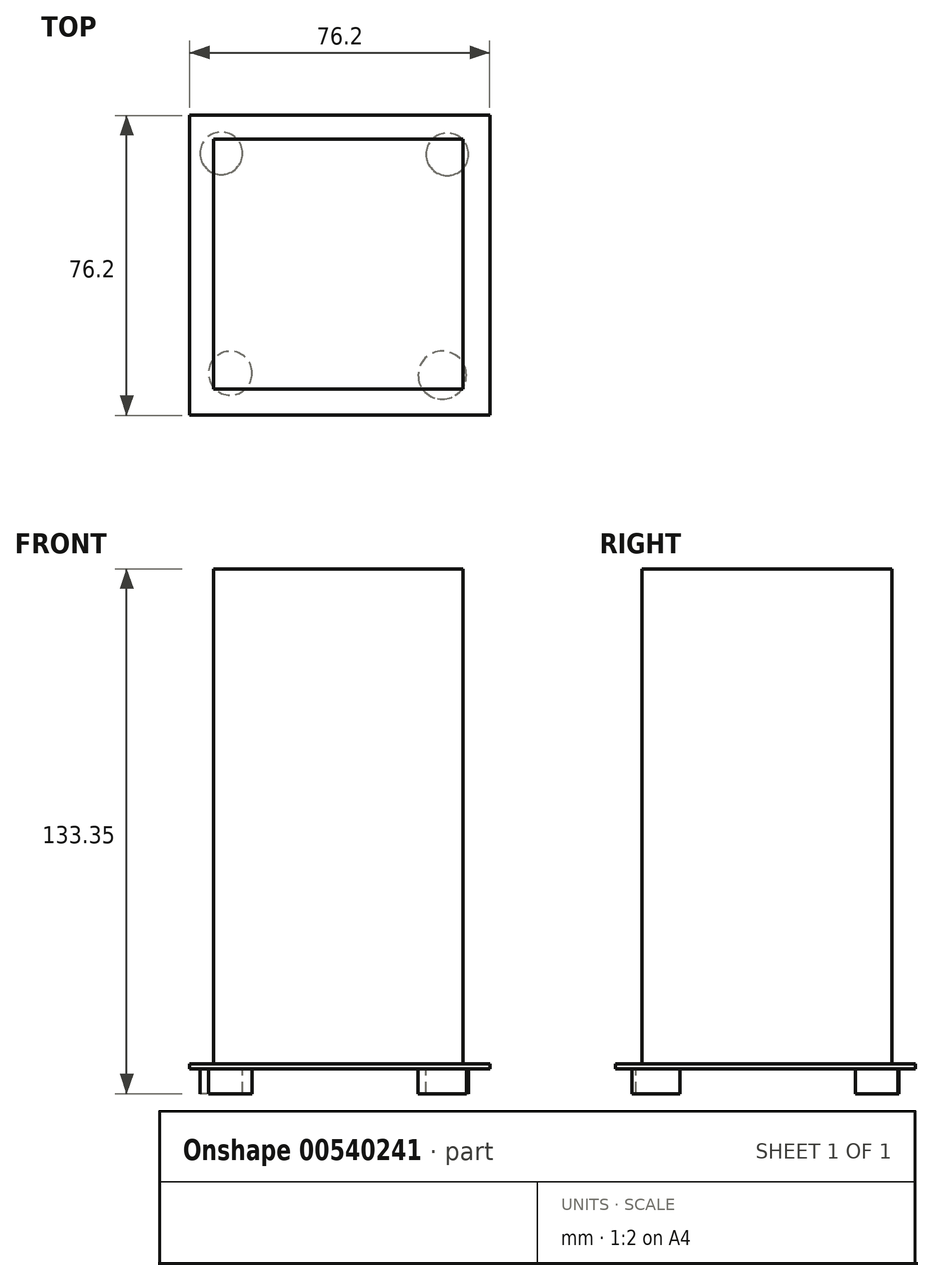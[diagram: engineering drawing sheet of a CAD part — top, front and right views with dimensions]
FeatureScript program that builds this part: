
annotation { "Feature Type Name" : "Feature", "Feature Type Description" : "" }
export const myFeature = defineFeature(function(context is Context, id is Id, definition is map)
    precondition{}
    {
        {
            var Q0;
            Q0=qCreatedBy(makeId("Top.planeOp"),FACE);
            var sketch = newSketch(context, id + "F0", { "sketchPlane" : qUnion([Q0])});
            skLineSegment(sketch, "E0", {"start": v(-36.96, -32.03) * mm, "end": v(39.24, -32.03) * mm});
            skLineSegment(sketch, "E1", {"start": v(39.24, -32.03) * mm, "end": v(39.24, 44.17) * mm});
            skLineSegment(sketch, "E2", {"start": v(39.24, 44.17) * mm, "end": v(-36.96, 44.17) * mm});
            skLineSegment(sketch, "E3", {"start": v(-36.96, 44.17) * mm, "end": v(-36.96, -32.03) * mm});
            skLineSegment(sketch, "E4.bottom", {"start": v(-30.6, -25.68) * mm, "end": v(32.9, -25.68) * mm});
            skLineSegment(sketch, "E4.top", {"start": v(-30.6, 37.82) * mm, "end": v(32.9, 37.82) * mm});
            skLineSegment(sketch, "E4.left", {"start": v(-30.6, -25.68) * mm, "end": v(-30.6, 37.82) * mm});
            skLineSegment(sketch, "E4.right", {"start": v(32.9, -25.68) * mm, "end": v(32.9, 37.82) * mm});
            skSolve(sketch);
        }
        {
            var Q0;
            Q0=qCreatedBy(makeId("Front.planeOp"),FACE);
            var sketch = newSketch(context, id + "F1", { "sketchPlane" : qUnion([Q0])});
            skLineSegment(sketch, "E5", {"start": v(-30.9, 0) * mm, "end": v(32.41, 0) * mm});
            skLineSegment(sketch, "E6", {"start": v(32.41, 0) * mm, "end": v(32.41, 127) * mm});
            skLineSegment(sketch, "E7", {"start": v(-30.9, 0) * mm, "end": v(-30.9, 127) * mm});
            skLineSegment(sketch, "E8", {"start": v(-30.9, 127) * mm, "end": v(32.41, 127) * mm});
            skSolve(sketch);
        }
        {
            var Q0;
            Q0=makeQuery(id+"F1.imprint","IMPRINT",FACE,{"disambiguationData":[TD([[makeQuery(id+"F1.imprint","IMPRINT",EDGE,{"derivedFrom":sQuery(id+"F1.wireOp",EDGE,"E5")}),1.0]])]});
            extrude(context, id + "F2", {"entities" : qUnion([Q0]), "depth" : 25.4 * mm, "offsetDistance" : 25.4 * mm});
        }
        {
            var Q0;
            Q0=makeQuery(id+"F2.opExtrude","CAP_FACE",FACE,{"disambiguationData":[OSD([sQuery(id+"F1.wireOp",EDGE,"E5"),sQuery(id+"F1.wireOp",EDGE,"E6"),sQuery(id+"F1.wireOp",EDGE,"E7"),sQuery(id+"F1.wireOp",EDGE,"E8")])],"isStart":true});
            extrude(context, id + "F3", {"entities" : qUnion([Q0]), "operationType" : NewBodyOperationType.ADD, "depth" : 38.1 * mm, "offsetDistance" : 25.4 * mm});
        }
        {
            var Q0;
            Q0=makeQuery(id+"F0.imprint","IMPRINT",FACE,{"disambiguationData":[TD([[makeQuery(id+"F0.imprint","IMPRINT",EDGE,{"derivedFrom":sQuery(id+"F0.wireOp",EDGE,"E0")}),1.0]])]});
            var Q1;
            Q1=makeQuery(id+"F0.imprint","IMPRINT",FACE,{"disambiguationData":[TD([[makeQuery(id+"F0.imprint","IMPRINT",EDGE,{"derivedFrom":sQuery(id+"F0.wireOp",EDGE,"E4.bottom")}),1.0]])]});
            extrude(context, id + "F4", {"entities" : qUnion([Q0, Q1]), "operationType" : NewBodyOperationType.ADD, "depth" : 1.27 * mm, "offsetDistance" : 25.4 * mm});
        }
        {
            var Q0;
            {var subQ0=sQuery(id+"F1.wireOp",EDGE,"E5");Q0=makeQuery(id+"F4.boolean.opBoolean","MERGE",FACE,{"derivedFrom":[makeQuery(id+"F3.boolean.opBoolean","MERGE",FACE,{"derivedFrom":[makeQuery(id+"F2.opExtrude","SWEPT_FACE",FACE,{"disambiguationData":[OSD([subQ0])]}),makeQuery(id+"F3.opExtrude","SWEPT_FACE",FACE,{"disambiguationData":[OSD([subQ0])]})]}),makeQuery(id+"F4.opExtrude","CAP_FACE",FACE,{"disambiguationData":[OSD([sQuery(id+"F0.wireOp",EDGE,"E0"),sQuery(id+"F0.wireOp",EDGE,"E1"),sQuery(id+"F0.wireOp",EDGE,"E2"),sQuery(id+"F0.wireOp",EDGE,"E3")])],"isStart":true})]});}
            var sketch = newSketch(context, id + "F5", { "sketchPlane" : qUnion([Q0])});
            skCircle(sketch, "E9", {"center": v(-26.67, 21.33) * mm, "radius": 5.57 * mm});
            skCircle(sketch, "E10", {"center": v(27.18, 21.84) * mm, "radius": 6.12 * mm});
            skCircle(sketch, "E11", {"center": v(28.45, -34.3) * mm, "radius": 5.4 * mm});
            skCircle(sketch, "E12", {"center": v(-28.96, -34.55) * mm, "radius": 5.4 * mm});
            skSolve(sketch);
        }
        {
            var Q0;
            Q0=makeQuery(id+"F5.imprint","IMPRINT",FACE,{"disambiguationData":[TD([[makeQuery(id+"F5.imprint","IMPRINT",EDGE,{"derivedFrom":sQuery(id+"F5.wireOp",EDGE,"E9")}),1.0]])]});
            var Q1;
            Q1=makeQuery(id+"F5.imprint","IMPRINT",FACE,{"disambiguationData":[TD([[makeQuery(id+"F5.imprint","IMPRINT",EDGE,{"derivedFrom":sQuery(id+"F5.wireOp",EDGE,"E10")}),1.0]])]});
            var Q2;
            Q2=makeQuery(id+"F5.imprint","IMPRINT",FACE,{"disambiguationData":[TD([[makeQuery(id+"F5.imprint","IMPRINT",EDGE,{"derivedFrom":sQuery(id+"F5.wireOp",EDGE,"E11")}),1.0]])]});
            var Q3;
            Q3=makeQuery(id+"F5.imprint","IMPRINT",FACE,{"disambiguationData":[TD([[makeQuery(id+"F5.imprint","IMPRINT",EDGE,{"derivedFrom":sQuery(id+"F5.wireOp",EDGE,"E12")}),1.0]])]});
            extrude(context, id + "F6", {"entities" : qUnion([Q0, Q1, Q2, Q3]), "operationType" : NewBodyOperationType.ADD, "depth" : 6.35 * mm, "offsetDistance" : 25.4 * mm});
        }
    });
